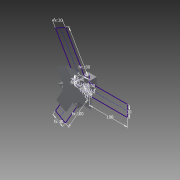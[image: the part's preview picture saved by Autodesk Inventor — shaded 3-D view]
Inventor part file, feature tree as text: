
AUTODESK INVENTOR PART (.ipt)
format: ipt  version: 2015 (Build 190159000, 159)  size: 135,680 bytes
history: native  units: mm
features: extrude x4, sketch x2, pattern_circular x1, projected_geometry x1
ambient origin geometry x8: Origin, YZ Plane, XZ Plane, XY Plane, X Axis, Y Axis, Z Axis, Center Point
bodies: Solid1 (feature_tree)
feature tree (8):
  sketch  "Sketch1"  dims[d1=25.4mm d2=30.0mm]
  extrude  "Extrusion1"  Depth=30.0mm
  extrude  "Extrusion2"  Depth=30.0mm
  pattern_circular  "Circular Pattern1"  Count=10  [1 undecoded]
  extrude  "Extrusion3"  TaperAngle=120.0deg  [1 undecoded]
  extrude  "Extrusion4"  Depth=30.0mm
  sketch  "Sketch2"  dims[d3=100.0mm d4=30.0mm d5=100.0mm d6=120.0deg d7=30.0mm d8=100.0mm d9=120.0deg d10=23.0mm d11=30.0mm d12=0.0mm d13=6.981317mm d14=100.0mm d15=0.0mm d16=30.0mm d17=360.0deg d19=25.4mm d20=0.0mm d21=5.0mm d22=24.0mm d23=5.0mm d24=5.0mm d25=24.0mm d26=24.0mm d27=25.4mm d28=0.0mm]
  projected_geometry  "Projected Loop1"
note: 2 required parameter values undecoded (feature->parameter linkage not recoverable at this tier; creation-order binding heuristic only, values carry confidence <= 0.55)
